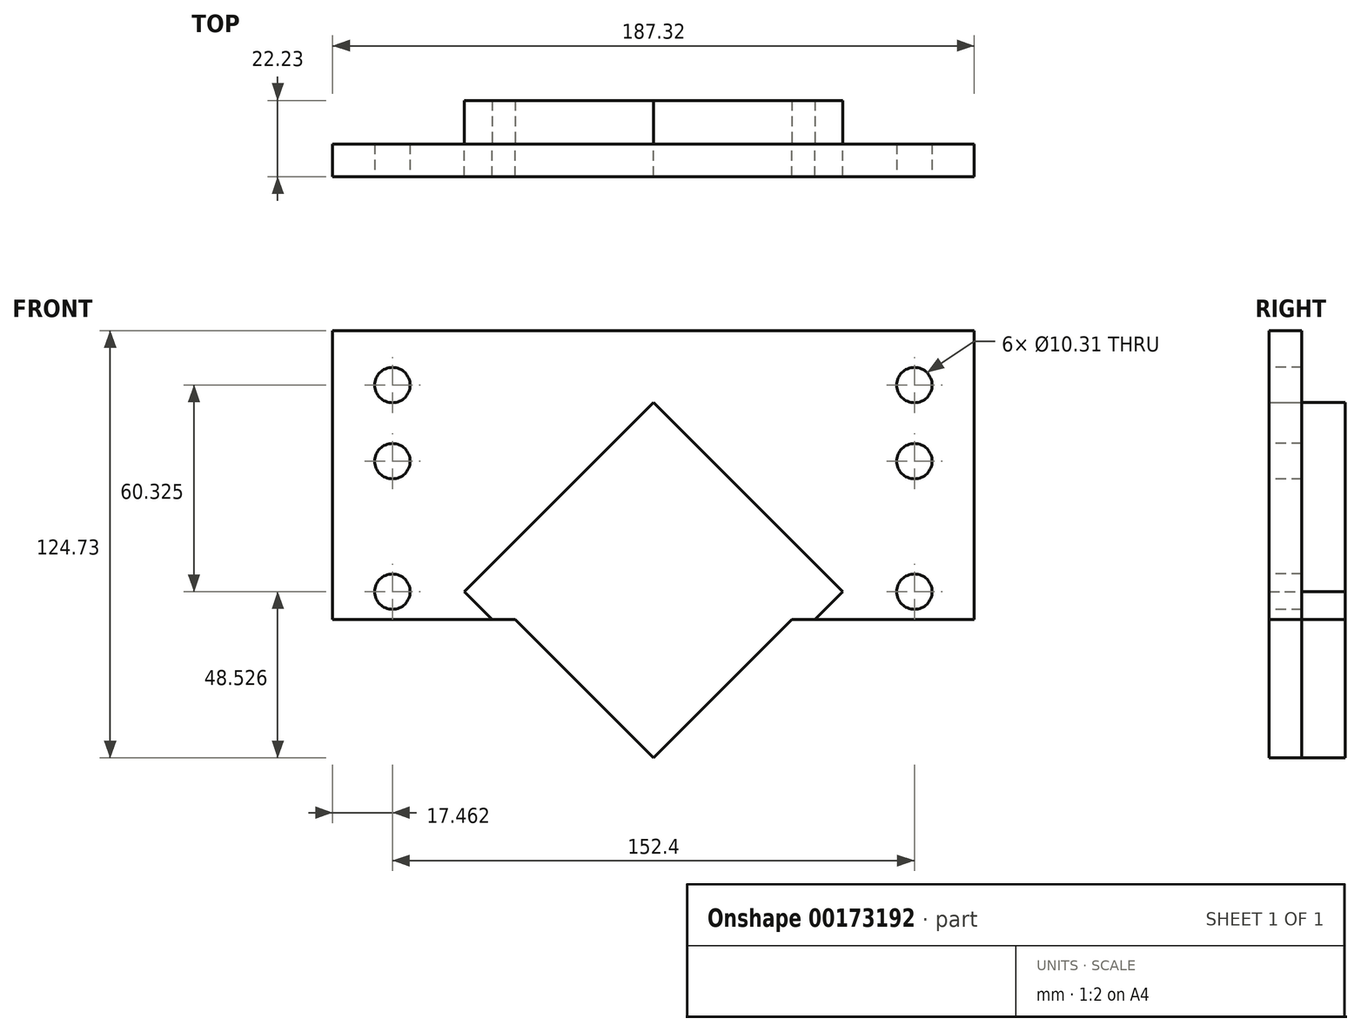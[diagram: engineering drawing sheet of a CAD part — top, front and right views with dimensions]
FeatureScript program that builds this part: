
annotation { "Feature Type Name" : "Feature", "Feature Type Description" : "" }
export const myFeature = defineFeature(function(context is Context, id is Id, definition is map)
    precondition{}
    {
        {
            var Q0;
            Q0=qCreatedBy(makeId("Front.planeOp"),FACE);
            var sketch = newSketch(context, id + "F0", { "sketchPlane" : qUnion([Q0])});
            skLineSegment(sketch, "E0.bottom", {"start": v(-76.3, 64.06) * mm, "end": v(111.02, 64.06) * mm});
            skLineSegment(sketch, "E0.left", {"start": v(-76.3, 64.06) * mm, "end": v(-76.3, -20.26) * mm});
            skLineSegment(sketch, "E0.right", {"start": v(111.02, 64.06) * mm, "end": v(111.02, -20.26) * mm});
            skPoint(sketch, "E1", {"position": v(-58.84, -12.14) * mm});
            skPoint(sketch, "E2", {"position": v(-58.84, -50.24) * mm});
            skPoint(sketch, "E3", {"position": v(-58.84, -72.47) * mm});
            skPoint(sketch, "E4", {"position": v(-58.84, 25.96) * mm});
            skPoint(sketch, "E5", {"position": v(-58.84, 48.18) * mm});
            skPoint(sketch, "E6", {"position": v(93.56, 48.18) * mm});
            skPoint(sketch, "E7", {"position": v(93.56, 25.96) * mm});
            skPoint(sketch, "E8", {"position": v(93.56, -12.14) * mm});
            skPoint(sketch, "E9", {"position": v(93.56, -50.24) * mm});
            skPoint(sketch, "E10", {"position": v(93.56, -72.47) * mm});
            skPoint(sketch, "E11", {"position": v(17.4, -12.18) * mm});
            skPoint(sketch, "E12.visualSharp", {"position": v(17.4, 45.3) * mm});
            skPoint(sketch, "E13.visualSharp", {"position": v(74.87, -12.18) * mm});
            skPoint(sketch, "E14.visualSharp", {"position": v(17.4, -69.65) * mm});
            skArc(sketch, "E14.filletArc", {"start": v(16.27, -68.53) * mm, "mid": v(17.4, -69) * mm, "end": v(18.52, -68.53) * mm});
            skPoint(sketch, "E15.visualSharp", {"position": v(-40.08, -12.18) * mm});
            skLineSegment(sketch, "E16", {"start": v(17.4, -12.18) * mm, "end": v(50.83, -12.18) * mm});
            skLineSegment(sketch, "E17", {"start": v(17.4, -12.18) * mm, "end": v(-12.52, -12.18) * mm});
            skLineSegment(sketch, "E18.0", {"start": v(57.8, -20.26) * mm, "end": v(17.4, -60.67) * mm});
            skLineSegment(sketch, "E19.0", {"start": v(-23.02, -20.26) * mm, "end": v(17.4, -60.67) * mm});
            skLineSegment(sketch, "E20", {"start": v(-23.02, -20.26) * mm, "end": v(-76.3, -20.26) * mm});
            skLineSegment(sketch, "E21", {"start": v(57.8, -20.26) * mm, "end": v(111.02, -20.26) * mm});
            skPoint(sketch, "E0.top.end.orphan", {"position": v(111.02, -88.34) * mm});
            skPoint(sketch, "E22.orphan", {"position": v(-76.3, -88.34) * mm});
            skLineSegment(sketch, "E23.0", {"start": v(17.4, 43.05) * mm, "end": v(-37.83, -12.18) * mm});
            skLineSegment(sketch, "E24.0", {"start": v(17.4, 43.05) * mm, "end": v(72.62, -12.18) * mm});
            skLineSegment(sketch, "E25.0", {"start": v(72.62, -12.18) * mm, "end": v(64.54, -20.26) * mm});
            skLineSegment(sketch, "E26.0", {"start": v(-37.83, -12.18) * mm, "end": v(-29.75, -20.26) * mm});
            skSolve(sketch);
        }
        {
            var Q0;
            {var subQ1=sQuery(id+"F0.wireOp",EDGE,"E18.0");Q0=makeQuery(id+"F0.imprint","IMPRINT",FACE,{"disambiguationData":[TD([[makeQuery(id+"F0.imprint","IMPRINT",EDGE,{"derivedFrom":subQ1}),-1.0]])]});}
            extrude(context, id + "F1", {"entities" : qUnion([Q0]), "oppositeDirection" : true, "depth" : 12.7 * mm});
        }
        {
            var Q0;
            Q0=makeQuery(id+"F0.imprint","IMPRINT",FACE,{"disambiguationData":[TD([[makeQuery(id+"F0.imprint","IMPRINT",EDGE,{"derivedFrom":sQuery(id+"F0.wireOp",EDGE,"E0.bottom")}),-1.0]])]});
            extrude(context, id + "F2", {"entities" : qUnion([Q0]), "depth" : 9.52 * mm});
        }
        {
            var Q0;
            {var subQ1=sQuery(id+"F0.wireOp",EDGE,"E18.0");Q0=makeQuery(id+"F0.imprint","IMPRINT",FACE,{"disambiguationData":[TD([[makeQuery(id+"F0.imprint","IMPRINT",EDGE,{"derivedFrom":subQ1}),-1.0]])]});}
            extrude(context, id + "F3", {"entities" : qUnion([Q0]), "depth" : 9.52 * mm});
        }
        {
            var Q0;
            Q0=sQuery(id+"F0.wireOp",VERTEX,"E5");
            var Q1;
            Q1=sQuery(id+"F0.wireOp",VERTEX,"E4");
            var Q2;
            Q2=sQuery(id+"F0.wireOp",VERTEX,"E1");
            var Q3;
            Q3=sQuery(id+"F0.wireOp",VERTEX,"E6");
            var Q4;
            Q4=sQuery(id+"F0.wireOp",VERTEX,"E7");
            var Q5;
            Q5=sQuery(id+"F0.wireOp",VERTEX,"E8");
            var Q6;
            Q6=makeQuery(id+"F2.opExtrude","SWEPT_BODY",BODY,{"disambiguationData":[OSD([sQuery(id+"F0.wireOp",EDGE,"E0.bottom"),sQuery(id+"F0.wireOp",EDGE,"E0.left"),sQuery(id+"F0.wireOp",EDGE,"E0.right"),sQuery(id+"F0.wireOp",EDGE,"E20"),sQuery(id+"F0.wireOp",EDGE,"E21"),sQuery(id+"F0.wireOp",EDGE,"E23.0"),sQuery(id+"F0.wireOp",EDGE,"E24.0"),sQuery(id+"F0.wireOp",EDGE,"E25.0"),sQuery(id+"F0.wireOp",EDGE,"E26.0")])]});
            hole(context, id + "F4", {"style" : HoleStyle.SIMPLE, "endStyle" : HoleEndStyle.THROUGH, "oppositeDirection" : true, "holeDiameter" : 10.3 * mm, "isTappedThrough" : true, "tappedDepth" : 12.7 * mm, "tapClearance" : 3, "startFromSketch" : true, "locations" : qUnion([Q0, Q1, Q2, Q3, Q4, Q5]), "scope" : qUnion([Q6])});
        }
    });
